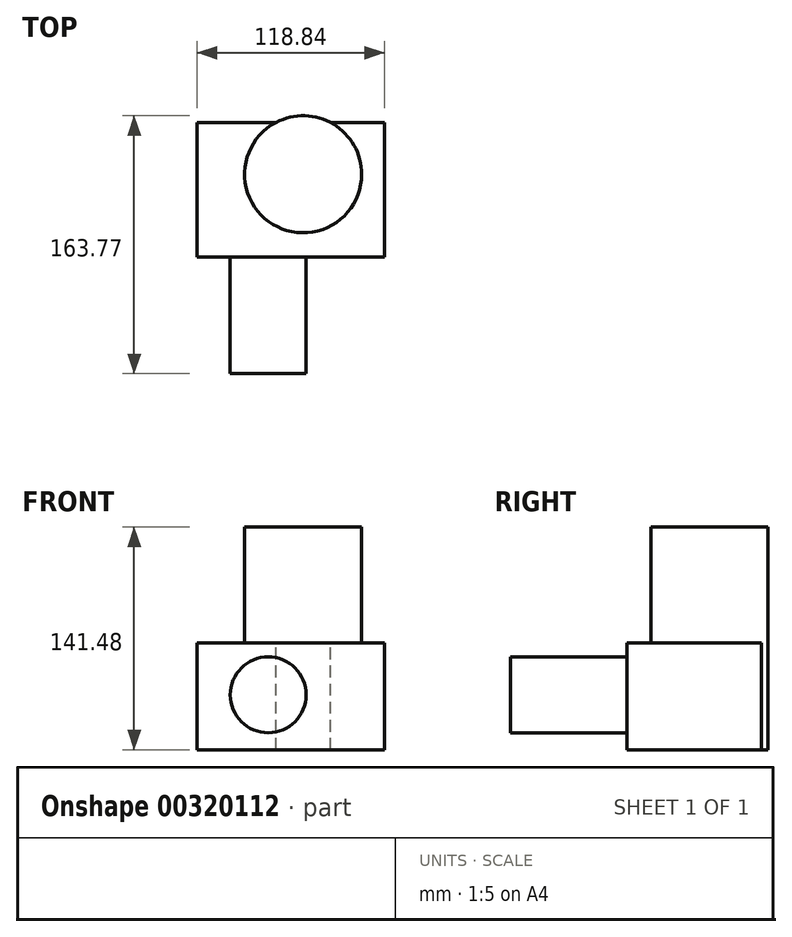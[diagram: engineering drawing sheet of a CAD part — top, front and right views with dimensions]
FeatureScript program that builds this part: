
annotation { "Feature Type Name" : "Feature", "Feature Type Description" : "" }
export const myFeature = defineFeature(function(context is Context, id is Id, definition is map)
    precondition{}
    {
        {
            var Q0;
            Q0=qCreatedBy(makeId("Top.planeOp"),FACE);
            var sketch = newSketch(context, id + "F0", { "sketchPlane" : qUnion([Q0])});
            skCircle(sketch, "E0", {"center": v(0, 4.08) * mm, "radius": 37.18 * mm});
            skSolve(sketch);
        }
        {
            var Q0;
            Q0=makeQuery(id+"F0.imprint","IMPRINT",FACE,{"disambiguationData":[TD([[makeQuery(id+"F0.imprint","IMPRINT",EDGE,{"derivedFrom":sQuery(id+"F0.wireOp",EDGE,"E0")}),1.0]])]});
            extrude(context, id + "F1", {"entities" : qUnion([Q0]), "depth" : 73.66 * mm});
        }
        {
            var Q0;
            Q0=makeQuery(id+"F0.imprint","IMPRINT",FACE,{"disambiguationData":[TD([[makeQuery(id+"F0.imprint","IMPRINT",EDGE,{"derivedFrom":sQuery(id+"F0.wireOp",EDGE,"E0")}),1.0]])]});
            var sketch = newSketch(context, id + "F2", { "sketchPlane" : qUnion([Q0])});
            skLineSegment(sketch, "E1.bottom", {"start": v(-67.25, 36.98) * mm, "end": v(51.6, 36.98) * mm});
            skLineSegment(sketch, "E1.top", {"start": v(-67.25, -48.6) * mm, "end": v(51.6, -48.6) * mm});
            skLineSegment(sketch, "E1.left", {"start": v(-67.25, 36.98) * mm, "end": v(-67.25, -48.6) * mm});
            skLineSegment(sketch, "E1.right", {"start": v(51.6, 36.98) * mm, "end": v(51.6, -48.6) * mm});
            skSolve(sketch);
        }
        {
            var Q0;
            Q0=makeQuery(id+"F2.imprint","IMPRINT",FACE,{"disambiguationData":[TD([[makeQuery(id+"F2.imprint","IMPRINT",EDGE,{"derivedFrom":sQuery(id+"F2.wireOp",EDGE,"E1.top")}),1.0]])]});
            var Q1;
            Q1=makeQuery(id+"F0.imprint","IMPRINT",FACE,{"disambiguationData":[TD([[makeQuery(id+"F0.imprint","IMPRINT",EDGE,{"derivedFrom":sQuery(id+"F0.wireOp",EDGE,"E0")}),1.0]])]});
            extrude(context, id + "F3", {"entities" : qUnion([Q0, Q1]), "operationType" : NewBodyOperationType.ADD, "oppositeDirection" : true, "depth" : 67.82 * mm});
        }
        {
            var Q0;
            Q0=makeQuery(id+"F3.opExtrude","SWEPT_FACE",FACE,{"disambiguationData":[OSD([sQuery(id+"F2.wireOp",EDGE,"E1.top")])]});
            var sketch = newSketch(context, id + "F4", { "sketchPlane" : qUnion([Q0])});
            skCircle(sketch, "E2", {"center": v(-22.21, -32.92) * mm, "radius": 24.1 * mm});
            skSolve(sketch);
        }
        {
            var Q0;
            Q0=makeQuery(id+"F4.imprint","IMPRINT",FACE,{"disambiguationData":[TD([[makeQuery(id+"F4.imprint","IMPRINT",EDGE,{"derivedFrom":sQuery(id+"F4.wireOp",EDGE,"E2")}),1.0]])]});
            extrude(context, id + "F5", {"entities" : qUnion([Q0]), "operationType" : NewBodyOperationType.ADD, "depth" : 73.9 * mm});
        }
    });
